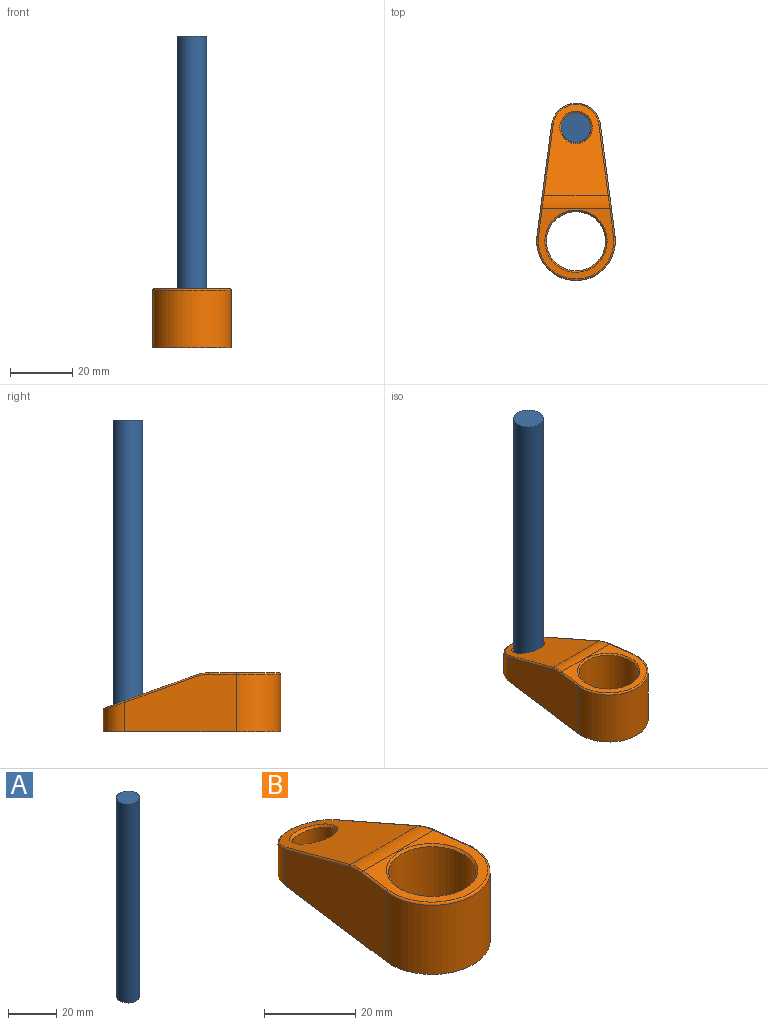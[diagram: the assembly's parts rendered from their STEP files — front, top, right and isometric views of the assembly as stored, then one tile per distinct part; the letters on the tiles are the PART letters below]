
ASSEMBLY  parts=2 mates=1
PART A: 3 faces, bbox 9.5x9.5x100.5 mm
  f0: cylinder r=4.76mm len=100.5mm, axis (0,0,-1), area 3007.2mm2, adj f1,f2
  f1: plane 9.53x9.53mm, normal (0,0,1), area 71.3mm2, adj f0
  f2: plane 9.53x9.53mm, normal (0,0,-1), area 71.3mm2, adj f0
PART B: 28 faces, bbox 29.1x59.8x20.7 mm
  f0: plane 57.15x25.4mm, normal (0,0,-1), area 513.9mm2, adj f1,f2,f3,f4,f5,f6,f21,f22
  f1: plane 35.89x18.54mm, normal (0.99,0.13,0), area 557.4mm2, adj f0,f2,f5,f10,f12,f14
  f2: cylinder r=7.94mm len=15.74mm, axis (0,0,-1), area 216.9mm2, adj f0,f1,f3,f16
  f3: plane 35.89x18.54mm, normal (-0.99,0.13,0), area 557.4mm2, adj f0,f2,f5,f13,f15,f17
  f4: cylinder r=4.76mm len=11.76mm, axis (0,0,-1), area 295.1mm2, adj f0,f18
  f5: cylinder r=12.7mm len=25.4mm, axis (0,0,-1), area 801.4mm2, adj f0,f1,f3,f11
  f6: cylinder r=9.53mm len=19.05mm, axis (0,0,-1), area 1109.7mm2, adj f0,f19
  f7: plane 24.38x22.65mm, normal (0,0,1), area 160mm2, adj f9,f10,f11,f13,f19
  f8: plane 29.33x20.76mm, normal (0,0.34,0.94), area 415.5mm2, adj f9,f14,f16,f17,f18
  f9: cylinder r=12.7mm len=21.84mm, axis (1,0,0), area 94.4mm2, adj f7,f8,f12,f15
  f10: cylinder r=0.51mm len=8.94mm, axis (0.13,-0.99,0), area 7.1mm2, adj f1,f7,f11,f12
  f11: torus R=12.19mm, axis (0,0,1), area 34mm2, adj f5,f7,f10,f13
  f12: bspline ~7.63x1.64mm, area 3.5mm2, adj f1,f9,f10,f14
  f13: cylinder r=0.51mm len=8.94mm, axis (0.13,0.99,0), area 7.1mm2, adj f3,f7,f11,f15
  f14: cylinder r=0.51mm len=22.97mm, axis (0.12,-0.93,0.34), area 19mm2, adj f1,f8,f12,f16
  f15: bspline ~7.63x1.64mm, area 3.5mm2, adj f3,f9,f13,f17
  f16: bspline ~15.74x6.9mm, area 15.5mm2, adj f2,f8,f14,f17
  f17: cylinder r=0.51mm len=22.97mm, axis (0.12,0.93,-0.34), area 19mm2, adj f3,f8,f15,f16
  f18: bspline ~10.54x10.54mm, area 23.3mm2, adj f4,f8
  f19: cone r=9.53mm half-angle=45deg, axis (0,0,1), area 44.1mm2, adj f6,f7
  f20: plane 1.13x0.88mm, normal (0,0,-1), area 0.4mm2, adj f21,f24,f27
  f21: plane 21.25x15.88mm, normal (-0.99,-0.13,0), area 275.8mm2, adj f0,f20,f23,f24,f26,f27
  f22: plane 21.25x15.88mm, normal (0.99,-0.13,0), area 275.8mm2, adj f0,f23,f24,f25,f26,f27
  f23: cylinder r=7.94mm len=11.09mm, axis (0,0,-1), area 111.4mm2, adj f0,f21,f22,f26
  f24: cylinder r=12.71mm len=16.68mm, axis (0,0,-1), area 288.8mm2, adj f0,f20,f21,f22,f25,f27
  f25: plane 1.13x0.88mm, normal (0,0,-1), area 0.4mm2, adj f22,f24,f27
  f26: plane 18.75x17.24mm, normal (0,-0.34,-0.94), area 224.6mm2, adj f21,f22,f23,f27
  f27: cylinder r=9.52mm len=16.45mm, axis (1,0,0), area 31.1mm2, adj f20,f21,f22,f24,f25,f26
PLACE A t=(43.1,30.63,0)mm
PLACE B at identity
MATE slider A.f0 <-> B.f2  axis (0,0,-1) through (0,36.51,0)mm
